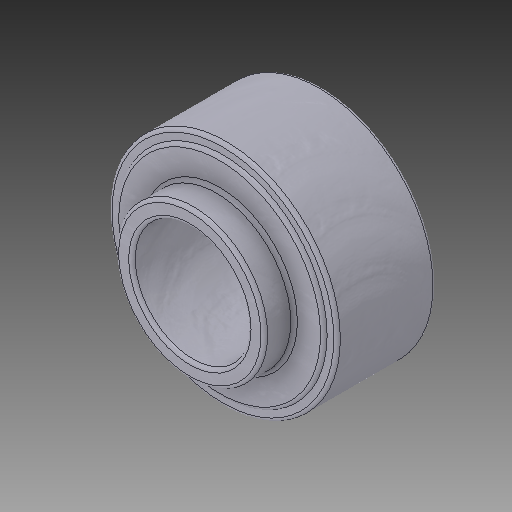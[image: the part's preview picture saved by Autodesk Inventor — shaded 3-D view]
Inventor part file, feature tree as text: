
AUTODESK INVENTOR PART (.ipt)
format: ipt  version: 2019 (Build 230136000, 136)  size: 220,160 bytes
history: native  units: in
note: dims shown in document units (in); Inventor stores cm internally (conversion verified against a paired STEP export)
features: sketch x6, other x3
ambient origin geometry x8: Origin, YZ Plane, XZ Plane, XY Plane, X Axis, Y Axis, Z Axis, Center Point
bodies: Solid1 (feature_tree)
feature tree (9):
  other  "project flange bearing part2_MIR1_MIR_MIR.ipt"
  other  "Solid1::project flange bearing part2_MIR1_MIR_MIR.ipt"
  other  "TaggingFeature1"
  sketch  "Sketch1"  dims[d0=0.3937in]
  sketch  "Sketch2"
  sketch  "Sketch3"
  sketch  "Sketch4"
  sketch  "Sketch5"
  sketch  "Sketch6"
